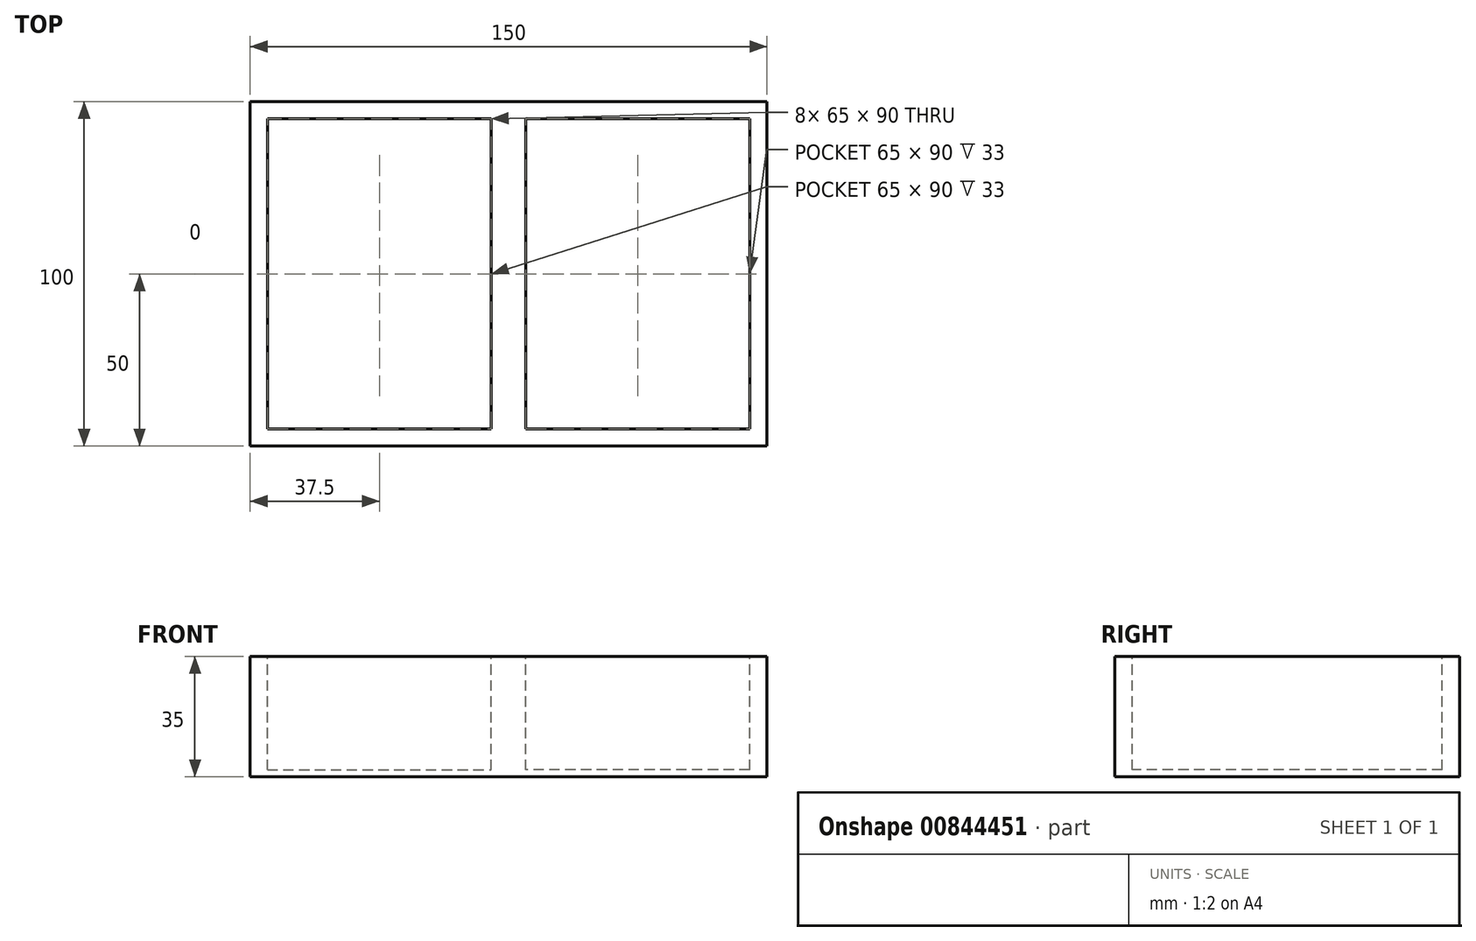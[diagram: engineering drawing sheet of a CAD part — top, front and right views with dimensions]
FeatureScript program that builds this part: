
annotation { "Feature Type Name" : "Feature", "Feature Type Description" : "" }
export const myFeature = defineFeature(function(context is Context, id is Id, definition is map)
    precondition{}
    {
        {
            var Q0;
            Q0=qCreatedBy(makeId("Top.planeOp"),FACE);
            var sketch = newSketch(context, id + "F0", { "sketchPlane" : qUnion([Q0])});
            skLineSegment(sketch, "E0.bottom", {"start": v(75, -50) * mm, "end": v(-75, -50) * mm});
            skLineSegment(sketch, "E0.top", {"start": v(75, 50) * mm, "end": v(-75, 50) * mm});
            skLineSegment(sketch, "E0.left", {"start": v(75, -50) * mm, "end": v(75, 50) * mm});
            skLineSegment(sketch, "E0.right", {"start": v(-75, -50) * mm, "end": v(-75, 50) * mm});
            skPoint(sketch, "E0.middle", {"position": v(0, 0) * mm});
            skSolve(sketch);
        }
        {
            var Q0;
            Q0=qSketchRegion(id+"F0",true);
            extrude(context, id + "F1", {"entities" : qUnion([Q0]), "depth" : 35 * mm, "offsetDistance" : 25 * mm});
        }
        {
            var Q0;
            Q0=makeQuery(id+"F1.opExtrude","CAP_FACE",FACE,{"disambiguationData":[OSD([sQuery(id+"F0.wireOp",EDGE,"E0.bottom"),sQuery(id+"F0.wireOp",EDGE,"E0.top"),sQuery(id+"F0.wireOp",EDGE,"E0.left"),sQuery(id+"F0.wireOp",EDGE,"E0.right")])],"isStart":false});
            var sketch = newSketch(context, id + "F2", { "sketchPlane" : qUnion([Q0])});
            skLineSegment(sketch, "E1.bottom", {"start": v(-70, 45) * mm, "end": v(-5, 45) * mm});
            skLineSegment(sketch, "E1.top", {"start": v(-70, -45) * mm, "end": v(-5, -45) * mm});
            skLineSegment(sketch, "E1.left", {"start": v(-70, 45) * mm, "end": v(-70, -45) * mm});
            skLineSegment(sketch, "E1.right", {"start": v(-5, 45) * mm, "end": v(-5, -45) * mm});
            skPoint(sketch, "E1.middle", {"position": v(-37.5, 0) * mm});
            skPoint(sketch, "E2", {"position": v(0, 50) * mm});
            skPoint(sketch, "E3", {"position": v(-37.5, 50) * mm});
            skLineSegment(sketch, "E4.MirrorCS", {"start": v(70, 45) * mm, "end": v(70, -45) * mm});
            skLineSegment(sketch, "E5.MirrorCS", {"start": v(70, -45) * mm, "end": v(5, -45) * mm});
            skLineSegment(sketch, "E6.MirrorCS", {"start": v(70, 45) * mm, "end": v(5, 45) * mm});
            skLineSegment(sketch, "E7.MirrorCS", {"start": v(5, 45) * mm, "end": v(5, -45) * mm});
            skSolve(sketch);
        }
        {
            var Q0;
            Q0=qSketchRegion(id+"F2",true);
            extrude(context, id + "F3", {"entities" : qUnion([Q0]), "operationType" : NewBodyOperationType.REMOVE, "oppositeDirection" : true, "depth" : 33 * mm, "offsetDistance" : 25 * mm});
        }
    });
